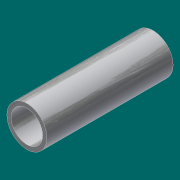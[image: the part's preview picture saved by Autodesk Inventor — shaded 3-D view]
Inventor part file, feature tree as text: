
AUTODESK INVENTOR PART (.ipt)
format: ipt  version: 2017 (Build 210142000, 142)  size: 87,552 bytes
history: native  units: in
note: dims shown in document units (in); Inventor stores cm internally (conversion verified against a paired STEP export)
features: extrude x1, sketch x1
ambient origin geometry x8: Origin, YZ Plane, XZ Plane, XY Plane, X Axis, Y Axis, Z Axis, Center Point
bodies: Solid1 (feature_tree)
feature tree (2):
  extrude  "Extrusion1"  Depth=6.0in
  sketch  "Sketch1"  dims[d0=1.9in d1=1.5in d2=6.0in d3=0.0in]
